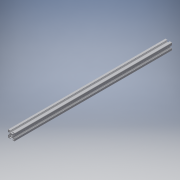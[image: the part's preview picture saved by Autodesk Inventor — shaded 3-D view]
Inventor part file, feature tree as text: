
AUTODESK INVENTOR PART (.ipt)
format: ipt  version: 2016 (Build 200138000, 138)  size: 300,544 bytes
history: native  units: in
note: dims shown in document units (in); Inventor stores cm internally (conversion verified against a paired STEP export)
features: other x3, extrude x1, sketch x1
ambient origin geometry x8: Origin, YZ Plane, XZ Plane, XY Plane, X Axis, Y Axis, Z Axis, Center Point
bodies: Solid1 (feature_tree)
feature tree (5):
  other  "Blocks"
  extrude  "Extrusion1"  [1 undecoded]
  sketch  "Sketch1"  dims[d1=0.0in]
  other  "20x20"
  other  "20x20:1"
note: 1 required parameter value undecoded (feature->parameter linkage not recoverable at this tier; creation-order binding heuristic only, values carry confidence <= 0.55)
